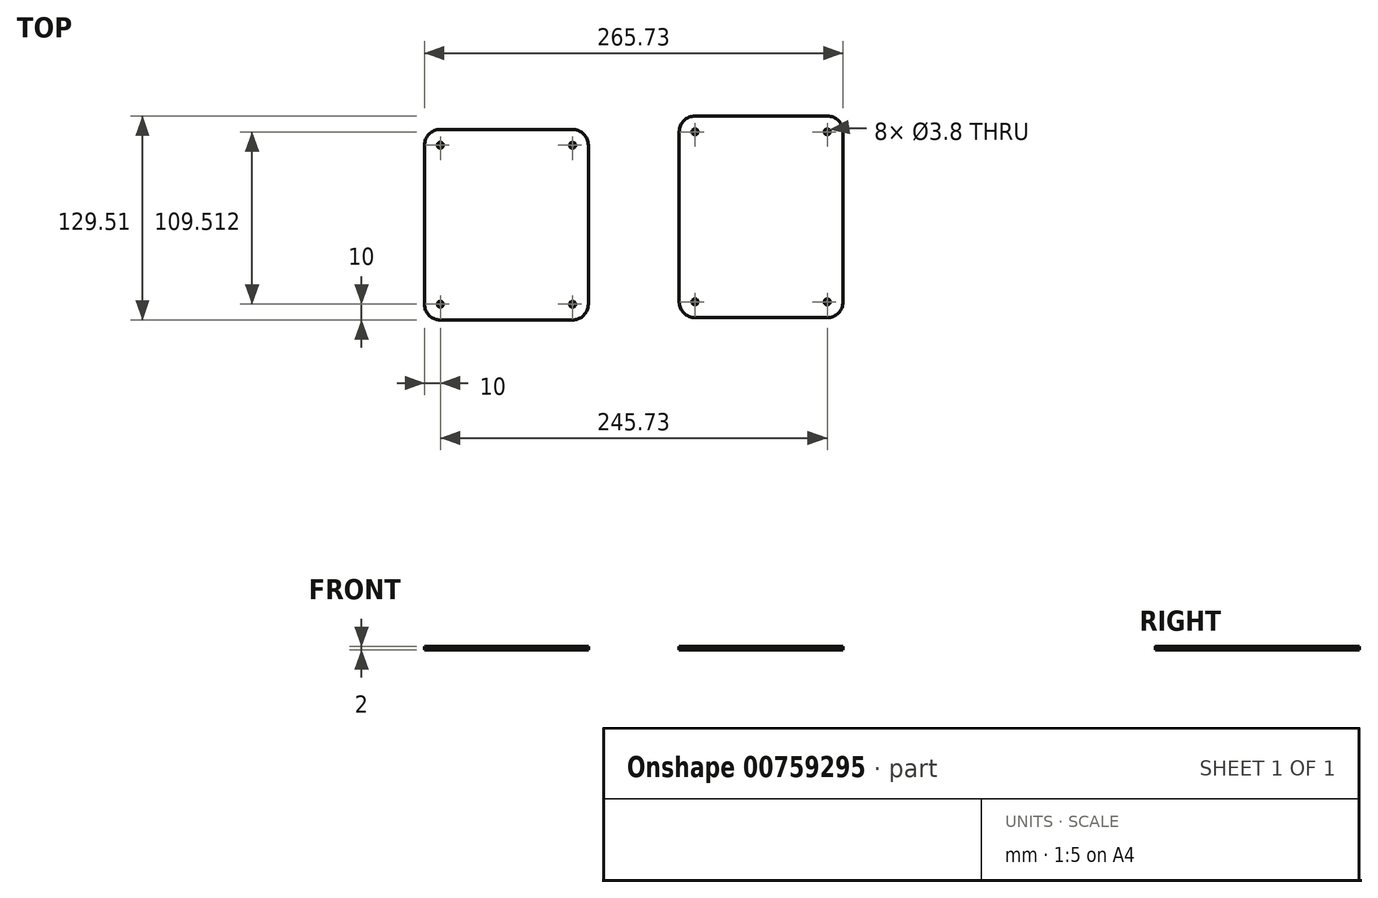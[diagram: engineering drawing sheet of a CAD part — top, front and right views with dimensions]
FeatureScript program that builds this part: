
annotation { "Feature Type Name" : "Feature", "Feature Type Description" : "" }
export const myFeature = defineFeature(function(context is Context, id is Id, definition is map)
    precondition{}
    {
        {
            var Q0;
            Q0=qCreatedBy(makeId("Top.planeOp"),FACE);
            var sketch = newSketch(context, id + "F0", { "sketchPlane" : qUnion([Q0])});
            skLineSegment(sketch, "E0.bottom", {"start": v(0, 0) * mm, "end": v(84, 0) * mm, "construction": true});
            skLineSegment(sketch, "E0.top", {"start": v(0, 101) * mm, "end": v(84, 101) * mm, "construction": true});
            skLineSegment(sketch, "E0.left", {"start": v(0, 0) * mm, "end": v(0, 101) * mm, "construction": true});
            skLineSegment(sketch, "E0.right", {"start": v(84, 0) * mm, "end": v(84, 101) * mm, "construction": true});
            skCircle(sketch, "E1", {"center": v(0, 0) * mm, "radius": 1.9 * mm});
            skCircle(sketch, "E2", {"center": v(84, 0) * mm, "radius": 1.9 * mm});
            skCircle(sketch, "E3", {"center": v(84, 101) * mm, "radius": 1.9 * mm});
            skCircle(sketch, "E4", {"center": v(0, 101) * mm, "radius": 1.9 * mm});
            skLineSegment(sketch, "E5.bottom", {"start": v(0, 111) * mm, "end": v(84, 111) * mm});
            skLineSegment(sketch, "E5.top", {"start": v(0, -10) * mm, "end": v(84, -10) * mm});
            skLineSegment(sketch, "E5.left", {"start": v(-10, 101) * mm, "end": v(-10, 0) * mm});
            skLineSegment(sketch, "E5.right", {"start": v(94, 101) * mm, "end": v(94, 0) * mm});
            skLineSegment(sketch, "E6", {"start": v(-10, -10) * mm, "end": v(0, 0) * mm, "construction": true});
            skLineSegment(sketch, "E7", {"start": v(94, -10) * mm, "end": v(84, 0) * mm, "construction": true});
            skLineSegment(sketch, "E8", {"start": v(94, 111) * mm, "end": v(84, 101) * mm, "construction": true});
            skLineSegment(sketch, "E9", {"start": v(-10, 111) * mm, "end": v(0, 101) * mm, "construction": true});
            skPoint(sketch, "E10.visualSharp", {"position": v(-10, 111) * mm});
            skArc(sketch, "E10.filletArc", {"start": v(0, 111) * mm, "mid": v(-7.07, 108.07) * mm, "end": v(-10, 101) * mm});
            skPoint(sketch, "E11.visualSharp", {"position": v(94, 111) * mm});
            skArc(sketch, "E11.filletArc", {"start": v(94, 101) * mm, "mid": v(91.07, 108.07) * mm, "end": v(84, 111) * mm});
            skPoint(sketch, "E12.visualSharp", {"position": v(94, -10) * mm});
            skArc(sketch, "E12.filletArc", {"start": v(84, -10) * mm, "mid": v(91.07, -7.07) * mm, "end": v(94, 0) * mm});
            skPoint(sketch, "E13.visualSharp", {"position": v(-10, -10) * mm});
            skArc(sketch, "E13.filletArc", {"start": v(-10, 0) * mm, "mid": v(-7.07, -7.07) * mm, "end": v(0, -10) * mm});
            skSolve(sketch);
        }
        {
            var Q0;
            Q0=makeQuery(id+"F0.imprint","IMPRINT",FACE,{"disambiguationData":[TD([[makeQuery(id+"F0.imprint","IMPRINT",EDGE,{"derivedFrom":sQuery(id+"F0.wireOp",EDGE,"E1")}),-1.0]])]});
            extrude(context, id + "F1", {"entities" : qUnion([Q0]), "depth" : 2 * mm, "offsetDistance" : 25.4 * mm});
        }
        {
            var Q0;
            Q0=qCreatedBy(makeId("Top.planeOp"),FACE);
            var sketch = newSketch(context, id + "F2", { "sketchPlane" : qUnion([Q0])});
            skLineSegment(sketch, "E14.bottom", {"start": v(161.73, 1.51) * mm, "end": v(245.73, 1.51) * mm, "construction": true});
            skLineSegment(sketch, "E14.top", {"start": v(161.73, 109.51) * mm, "end": v(245.73, 109.51) * mm, "construction": true});
            skLineSegment(sketch, "E14.left", {"start": v(161.73, 1.51) * mm, "end": v(161.73, 109.51) * mm, "construction": true});
            skLineSegment(sketch, "E14.right", {"start": v(245.73, 1.51) * mm, "end": v(245.73, 109.51) * mm, "construction": true});
            skCircle(sketch, "E15", {"center": v(161.73, 1.51) * mm, "radius": 1.9 * mm});
            skCircle(sketch, "E16", {"center": v(245.73, 1.51) * mm, "radius": 1.9 * mm});
            skCircle(sketch, "E17", {"center": v(245.73, 109.51) * mm, "radius": 1.9 * mm});
            skCircle(sketch, "E18", {"center": v(161.73, 109.51) * mm, "radius": 1.9 * mm});
            skLineSegment(sketch, "E19.bottom", {"start": v(161.73, 119.51) * mm, "end": v(245.73, 119.51) * mm});
            skLineSegment(sketch, "E19.top", {"start": v(161.73, -8.49) * mm, "end": v(245.73, -8.49) * mm});
            skLineSegment(sketch, "E19.left", {"start": v(151.73, 109.51) * mm, "end": v(151.73, 1.51) * mm});
            skLineSegment(sketch, "E19.right", {"start": v(255.73, 109.51) * mm, "end": v(255.73, 1.51) * mm});
            skLineSegment(sketch, "E20", {"start": v(151.73, -8.49) * mm, "end": v(161.73, 1.51) * mm, "construction": true});
            skLineSegment(sketch, "E21", {"start": v(255.73, -8.49) * mm, "end": v(245.73, 1.51) * mm, "construction": true});
            skLineSegment(sketch, "E22", {"start": v(255.73, 119.51) * mm, "end": v(245.73, 109.51) * mm, "construction": true});
            skLineSegment(sketch, "E23", {"start": v(151.73, 119.51) * mm, "end": v(161.73, 109.51) * mm, "construction": true});
            skPoint(sketch, "E24.visualSharp", {"position": v(151.73, 119.51) * mm});
            skArc(sketch, "E24.filletArc", {"start": v(161.73, 119.51) * mm, "mid": v(154.66, 116.58) * mm, "end": v(151.73, 109.51) * mm});
            skPoint(sketch, "E25.visualSharp", {"position": v(255.73, 119.51) * mm});
            skArc(sketch, "E25.filletArc", {"start": v(255.73, 109.51) * mm, "mid": v(252.8, 116.58) * mm, "end": v(245.73, 119.51) * mm});
            skPoint(sketch, "E26.visualSharp", {"position": v(255.73, -8.49) * mm});
            skArc(sketch, "E26.filletArc", {"start": v(245.73, -8.49) * mm, "mid": v(252.8, -5.56) * mm, "end": v(255.73, 1.51) * mm});
            skPoint(sketch, "E27.visualSharp", {"position": v(151.73, -8.49) * mm});
            skArc(sketch, "E27.filletArc", {"start": v(151.73, 1.51) * mm, "mid": v(154.66, -5.56) * mm, "end": v(161.73, -8.49) * mm});
            skSolve(sketch);
        }
        {
            var Q0;
            Q0 = qSketchRegion(id + "F2", true);
            extrude(context, id + "F3", {"entities" : qUnion([Q0]), "depth" : 2 * mm, "offsetDistance" : 25 * mm});
        }
    });
